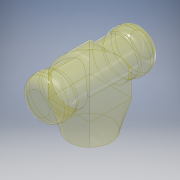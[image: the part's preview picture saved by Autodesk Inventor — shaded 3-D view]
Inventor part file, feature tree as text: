
AUTODESK INVENTOR PART (.ipt)
format: ipt  version: 2017 (Build 210142000, 142)  size: 241,664 bytes
history: native  units: mm
features: sketch x6, fillet x4, plane x3, loft x2, extrude x2, mirror x1
ambient origin geometry x8: Origin, YZ Plane, XZ Plane, XY Plane, X Axis, Y Axis, Z Axis, Center Point
bodies: Body1 (feature_tree)
feature tree (18):
  sketch  "Sketch2"  dims[d1=15.0mm d5=15.0mm]
  plane  "Work Plane1"
  loft  "Loft1"
  extrude  "Extrusion2"  TaperAngle=0.0deg  [1 undecoded]
  extrude  "Extrusion3"  Depth=15.0mm
  sketch  "Sketch6"  dims[d21=0.0mm d22=90.0deg]
  plane  "Work Plane2"
  loft  "Loft2"
  fillet  "Fillet1"  Radius=13.0mm
  fillet  "Fillet2"  Radius=5.0mm
  fillet  "Fillet3"  Radius=6.0mm
  plane  "Work Plane3"
  mirror  "Mirror1"
  fillet  "Fillet4"  [1 undecoded]
  sketch  "Sketch3"  dims[d6=15.0mm d7=0.0mm d8=90.0deg]
  sketch  "Sketch4"  dims[d9=0.0mm d10=90.0deg d11=15.0mm]
  sketch  "Sketch5"  dims[d12=15.0mm d13=15.0mm d14=0.0mm d15=13.0mm d16=5.0mm d17=0.0mm d18=6.0mm d19=0.0mm d20=90.0deg]
  sketch  "Sketch7"  dims[d23=2.0mm d24=15.0mm d25=3.0mm d26=5.0mm d27=7.25mm]
note: 2 required parameter values undecoded (feature->parameter linkage not recoverable at this tier; creation-order binding heuristic only, values carry confidence <= 0.55)
